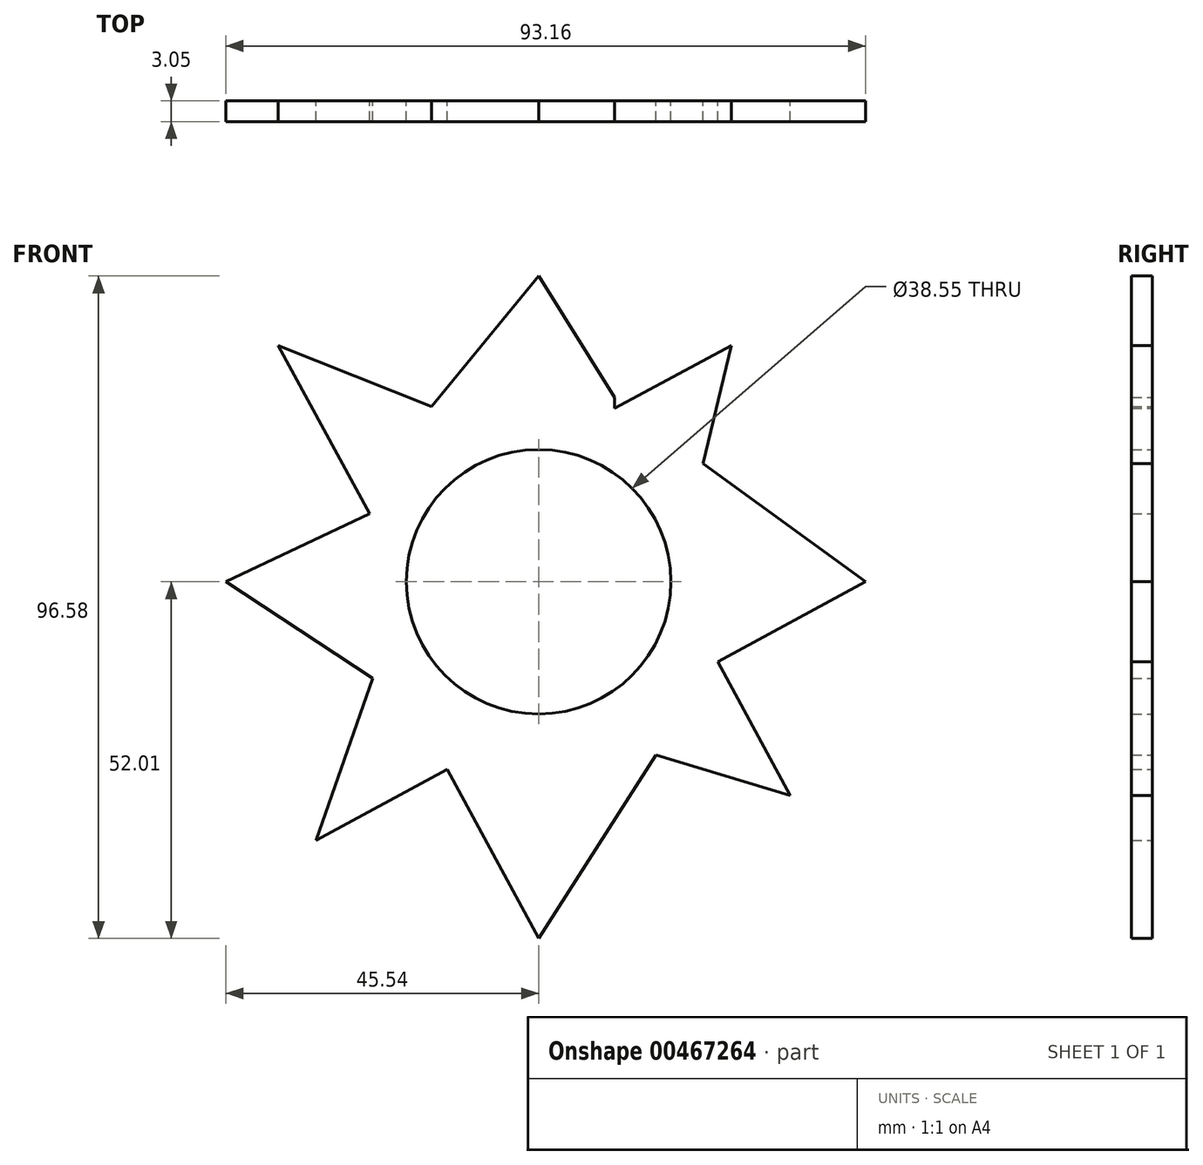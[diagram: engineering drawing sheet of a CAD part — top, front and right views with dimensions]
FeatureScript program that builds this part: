
annotation { "Feature Type Name" : "Feature", "Feature Type Description" : "" }
export const myFeature = defineFeature(function(context is Context, id is Id, definition is map)
    precondition{}
    {
        {
            var Q0;
            Q0=qCreatedBy(makeId("Front.planeOp"),FACE);
            var sketch = newSketch(context, id + "F0", { "sketchPlane" : qUnion([Q0])});
            skCircle(sketch, "E0", {"center": v(0, 0) * mm, "radius": 19.28 * mm});
            skLineSegment(sketch, "E1", {"start": v(-19.28, 0) * mm, "end": v(-37.93, 34.47) * mm});
            skLineSegment(sketch, "E2", {"start": v(-37.93, 34.47) * mm, "end": v(0, 19.28) * mm});
            skLineSegment(sketch, "E3", {"start": v(0, 19.28) * mm, "end": v(28.07, 34.47) * mm});
            skLineSegment(sketch, "E4", {"start": v(28.07, 34.47) * mm, "end": v(19.82, 0) * mm});
            skLineSegment(sketch, "E5", {"start": v(19.82, 0) * mm, "end": v(36.68, -31.15) * mm});
            skLineSegment(sketch, "E6", {"start": v(36.68, -31.15) * mm, "end": v(0, -20.13) * mm});
            skLineSegment(sketch, "E7", {"start": v(0, -20.13) * mm, "end": v(-32.45, -37.69) * mm});
            skLineSegment(sketch, "E8", {"start": v(-32.45, -37.69) * mm, "end": v(-19.28, 0) * mm});
            skLineSegment(sketch, "E9", {"start": v(23.95, 17.23) * mm, "end": v(47.62, 0) * mm});
            skLineSegment(sketch, "E10", {"start": v(47.62, 0) * mm, "end": v(26.12, -11.63) * mm});
            skLineSegment(sketch, "E11", {"start": v(-13.34, -27.35) * mm, "end": v(0, -52) * mm});
            skLineSegment(sketch, "E12", {"start": v(0, -52) * mm, "end": v(17.13, -25.27) * mm});
            skLineSegment(sketch, "E13", {"start": v(-24.2, -14.09) * mm, "end": v(-45.54, 0) * mm});
            skLineSegment(sketch, "E14", {"start": v(-45.54, 0) * mm, "end": v(-24.64, 9.9) * mm});
            skLineSegment(sketch, "E15", {"start": v(-15.62, 25.53) * mm, "end": v(0, 44.57) * mm});
            skLineSegment(sketch, "E16", {"start": v(0, 44.57) * mm, "end": v(11.07, 26.85) * mm});
            skLineSegment(sketch, "E17", {"start": v(11.07, 25.27) * mm, "end": v(11.07, 26.85) * mm});
            skSolve(sketch);
        }
        {
            var Q0;
            Q0 = qSketchRegion(id + "F0", true);
            extrude(context, id + "F1", {"entities" : qUnion([Q0]), "depth" : 3.05 * mm});
        }
    });
